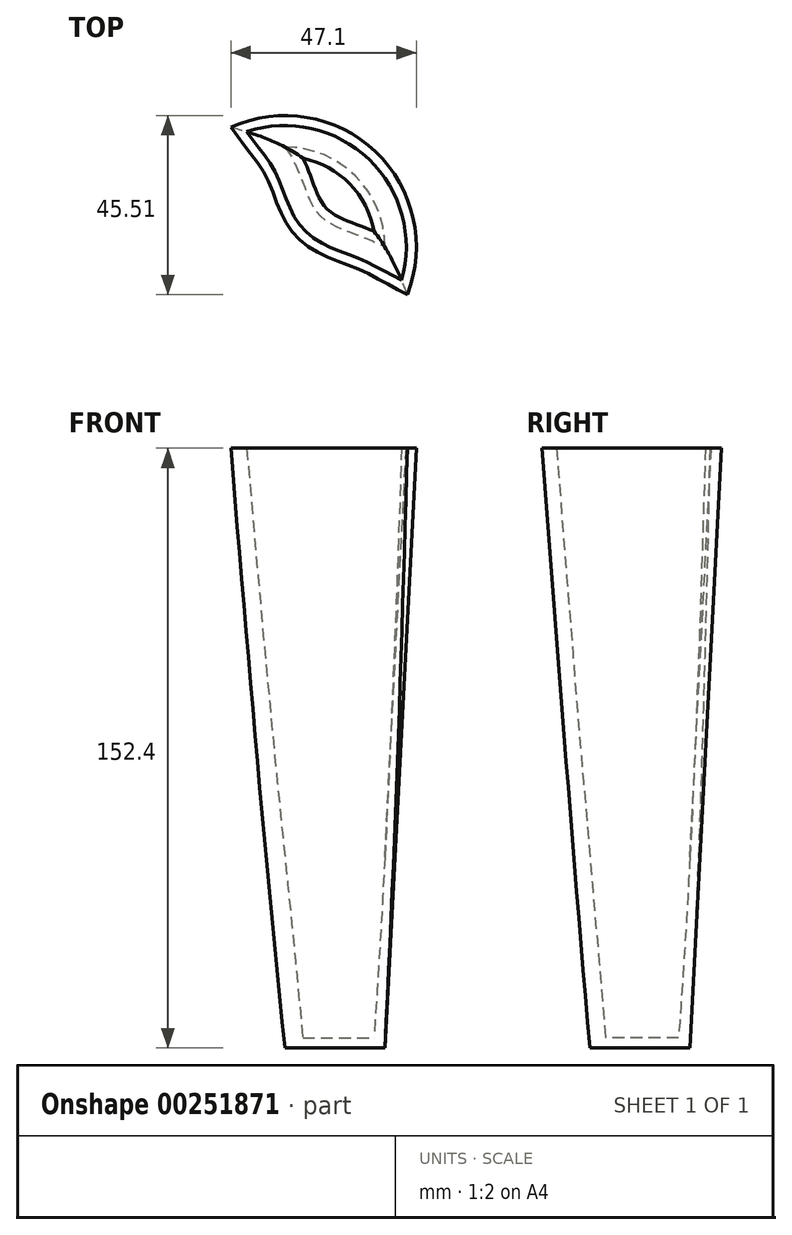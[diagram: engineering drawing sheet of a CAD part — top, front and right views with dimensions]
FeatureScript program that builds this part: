
annotation { "Feature Type Name" : "Feature", "Feature Type Description" : "" }
export const myFeature = defineFeature(function(context is Context, id is Id, definition is map)
    precondition{}
    {
        {
            var Q0;
            Q0=qCreatedBy(makeId("Top.planeOp"),FACE);
            var sketch = newSketch(context, id + "F0", { "sketchPlane" : qUnion([Q0])});
            skPoint(sketch, "E0.visualSharp", {"position": v(-75.02, 50.4) * mm});
            skPoint(sketch, "E1.visualSharp", {"position": v(77.38, 50.4) * mm});
            skArc(sketch, "E1.filletArc", {"start": v(77.38, 25) * mm, "mid": v(69.94, 42.96) * mm, "end": v(51.98, 50.4) * mm});
            skPoint(sketch, "E2.visualSharp", {"position": v(77.38, -51.2) * mm});
            skPoint(sketch, "E3.visualSharp", {"position": v(-75.02, -51.2) * mm});
            skArc(sketch, "E3.filletArc", {"start": v(-75.02, -25.8) * mm, "mid": v(-67.58, -43.76) * mm, "end": v(-49.62, -51.2) * mm});
            skFitSpline(sketch, "E4", {"points": [v(-75.02, 25) * mm, v(-49.62, 50.4) * mm, v(-41.37, 67.09) * mm, v(-12.6, 58.5) * mm, v(19.71, 65.31) * mm, v(51.98, 50.4) * mm, v(60.63, 33.29) * mm, v(77.38, 25) * mm, v(95.9, 0) * mm, v(87.31, -26.3) * mm, v(77.38, -25.8) * mm, v(64.48, -34.01) * mm, v(51.98, -51.2) * mm, v(7.85, -66.63) * mm, v(-49.62, -51.2) * mm, v(-75.02, -25.8) * mm, v(-96.8, 7.5) * mm, v(-75.02, 25) * mm]});
            skSolve(sketch);
        }
        {
            var Q0;
            Q0=makeQuery(id+"F0.imprint","IMPRINT",FACE,{"disambiguationData":[TD([[makeQuery(id+"F0.imprint","IMPRINT",EDGE,{"derivedFrom":sQuery(id+"F0.wireOp",EDGE,"E1.filletArc")}),1.0]])]});
            extrude(context, id + "F1", {"entities" : qUnion([Q0]), "depth" : 152.4 * mm, "hasDraft" : true, "draftAngle" : 3 * degree});
        }
        {
            var Q0;
            Q0=makeQuery(id+"F1.opExtrude","CAP_FACE",FACE,{"disambiguationData":[OSD([sQuery(id+"F0.wireOp",EDGE,"E1.filletArc"),sQuery(id+"F0.wireOp",EDGE,"E3.filletArc"),sQuery(id+"F0.wireOp",EDGE,"E4"),sQuery(id+"F0.wireOp",EDGE,"E4")])],"isStart":false});
            shell(context, id + "F2", {"entities" : qUnion([Q0]), "thickness" : 2.54 * mm});
        }
    });
